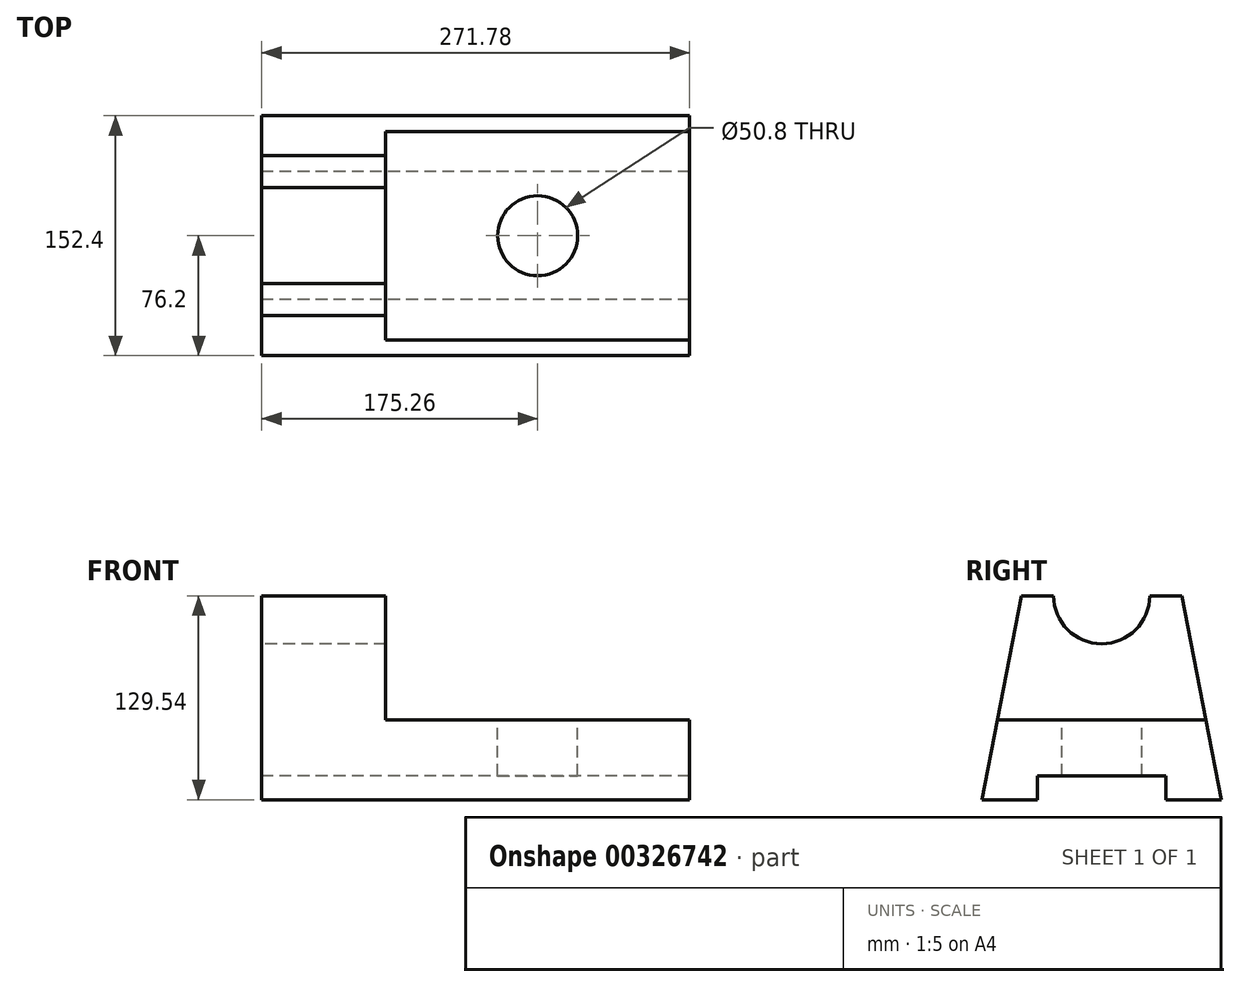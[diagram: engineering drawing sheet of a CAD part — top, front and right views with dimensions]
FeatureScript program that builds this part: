
annotation { "Feature Type Name" : "Feature", "Feature Type Description" : "" }
export const myFeature = defineFeature(function(context is Context, id is Id, definition is map)
    precondition{}
    {
        {
            var Q0;
            Q0=qCreatedBy(makeId("Right.planeOp"),FACE);
            var sketch = newSketch(context, id + "F0", { "sketchPlane" : qUnion([Q0])});
            skLineSegment(sketch, "E0", {"start": v(0, 139.55) * mm, "end": v(0, -97.42) * mm, "construction": true});
            skLineSegment(sketch, "E1", {"start": v(0, 0) * mm, "end": v(-40.64, 0) * mm});
            skLineSegment(sketch, "E2", {"start": v(-40.64, 0) * mm, "end": v(-40.64, -15.24) * mm});
            skLineSegment(sketch, "E3", {"start": v(-40.64, -15.24) * mm, "end": v(-76.2, -15.24) * mm});
            skLineSegment(sketch, "E4", {"start": v(-76.2, -15.24) * mm, "end": v(-50.8, 114.3) * mm});
            skLineSegment(sketch, "E5.MirrorCS", {"start": v(0, 0) * mm, "end": v(40.64, 0) * mm});
            skLineSegment(sketch, "E6.MirrorCS", {"start": v(40.64, 0) * mm, "end": v(40.64, -15.24) * mm});
            skLineSegment(sketch, "E7.MirrorCS", {"start": v(40.64, -15.24) * mm, "end": v(76.2, -15.24) * mm});
            skLineSegment(sketch, "E8.MirrorCS", {"start": v(76.2, -15.24) * mm, "end": v(50.8, 114.3) * mm});
            skArc(sketch, "E9", {"start": v(-30.48, 114.3) * mm, "mid": v(0, 83.82) * mm, "end": v(30.48, 114.3) * mm});
            skLineSegment(sketch, "E10", {"start": v(-50.8, 114.3) * mm, "end": v(-30.48, 114.3) * mm});
            skLineSegment(sketch, "E11", {"start": v(50.8, 114.3) * mm, "end": v(30.48, 114.3) * mm});
            skSolve(sketch);
        }
        {
            var Q0;
            Q0=makeQuery(id+"F0.imprint","IMPRINT",FACE,{"disambiguationData":[TD([[makeQuery(id+"F0.imprint","IMPRINT",EDGE,{"derivedFrom":sQuery(id+"F0.wireOp",EDGE,"E1")}),-1.0]])]});
            extrude(context, id + "F1", {"entities" : qUnion([Q0]), "depth" : 271.78 * mm});
        }
        {
            var Q0;
            Q0=makeQuery(id+"F1.opExtrude","SWEPT_FACE",FACE,{"disambiguationData":[OSD([sQuery(id+"F0.wireOp",EDGE,"E11")])]});
            var sketch = newSketch(context, id + "F2", { "sketchPlane" : qUnion([Q0])});
            skLineSegment(sketch, "E12.bottom", {"start": v(78.74, 76.2) * mm, "end": v(271.78, 76.2) * mm});
            skLineSegment(sketch, "E12.top", {"start": v(78.74, -76.2) * mm, "end": v(271.78, -76.2) * mm});
            skLineSegment(sketch, "E12.left", {"start": v(78.74, 76.2) * mm, "end": v(78.74, -76.2) * mm});
            skLineSegment(sketch, "E12.right", {"start": v(271.78, 76.2) * mm, "end": v(271.78, -76.2) * mm});
            skPoint(sketch, "E13.centerSnap0", {"position": v(78.74, 0) * mm});
            skSolve(sketch);
        }
        {
            var Q0;
            {var subQ0=sQuery(id+"F2.wireOp",EDGE,"E12.bottom");Q0=makeQuery(id+"F2.imprint","IMPRINT",FACE,{"disambiguationData":[TD([[makeQuery(id+"F2.imprint","IMPRINT",EDGE,{"derivedFrom":subQ0}),-1.0]])]});}
            var Q1;
            {var subQ0=sQuery(id+"F2.wireOp",EDGE,"E12.left");var subQ1=sQuery(id+"F0.wireOp",EDGE,"E11");var subQ2=makeQuery(id+"F1.opExtrude","SWEPT_EDGE",EDGE,{"disambiguationData":[OSD([sQuery(id+"F0.wireOp",EDGE,"E8.MirrorCS"),subQ1])]});var subQ3=makeQuery(id+"F2.imprint","INTERSECT",VERTEX,{"derivedFrom":[subQ2,subQ0]});Q1=makeQuery(id+"F2.imprint","IMPRINT",FACE,{"disambiguationData":[TD([[makeQuery(id+"F2.imprint","IMPRINT",EDGE,{"disambiguationData":[TD([[subQ3,-1.0]])],"derivedFrom":subQ0}),1.0]])]});}
            var Q2;
            {var subQ0=sQuery(id+"F2.wireOp",EDGE,"E12.top");Q2=makeQuery(id+"F2.imprint","IMPRINT",FACE,{"disambiguationData":[TD([[makeQuery(id+"F2.imprint","IMPRINT",EDGE,{"derivedFrom":subQ0}),1.0]])]});}
            extrude(context, id + "F3", {"entities" : qUnion([Q0, Q1, Q2]), "operationType" : NewBodyOperationType.REMOVE, "oppositeDirection" : true, "depth" : 78.74 * mm});
        }
        {
            var Q0;
            Q0=makeQuery(id+"F3.boolean.opBoolean","COPY",FACE,{"derivedFrom":makeQuery(id+"F3.opExtrude","CAP_FACE",FACE,{"disambiguationData":[OSD([sQuery(id+"F2.wireOp",EDGE,"E12.bottom"),sQuery(id+"F2.wireOp",EDGE,"E12.top"),sQuery(id+"F2.wireOp",EDGE,"E12.left"),sQuery(id+"F2.wireOp",EDGE,"E12.right")])],"isStart":false})});
            var sketch = newSketch(context, id + "F4", { "sketchPlane" : qUnion([Q0])});
            skCircle(sketch, "E14", {"center": v(175.26, 0) * mm, "radius": 25.4 * mm});
            skSolve(sketch);
        }
        {
            var Q0;
            Q0=makeQuery(id+"F4.imprint","IMPRINT",FACE,{"disambiguationData":[TD([[makeQuery(id+"F4.imprint","IMPRINT",EDGE,{"derivedFrom":sQuery(id+"F4.wireOp",EDGE,"E14")}),1.0]])]});
            extrude(context, id + "F5", {"entities" : qUnion([Q0]), "operationType" : NewBodyOperationType.REMOVE, "oppositeDirection" : true, "depth" : 76.2 * mm});
        }
    });
